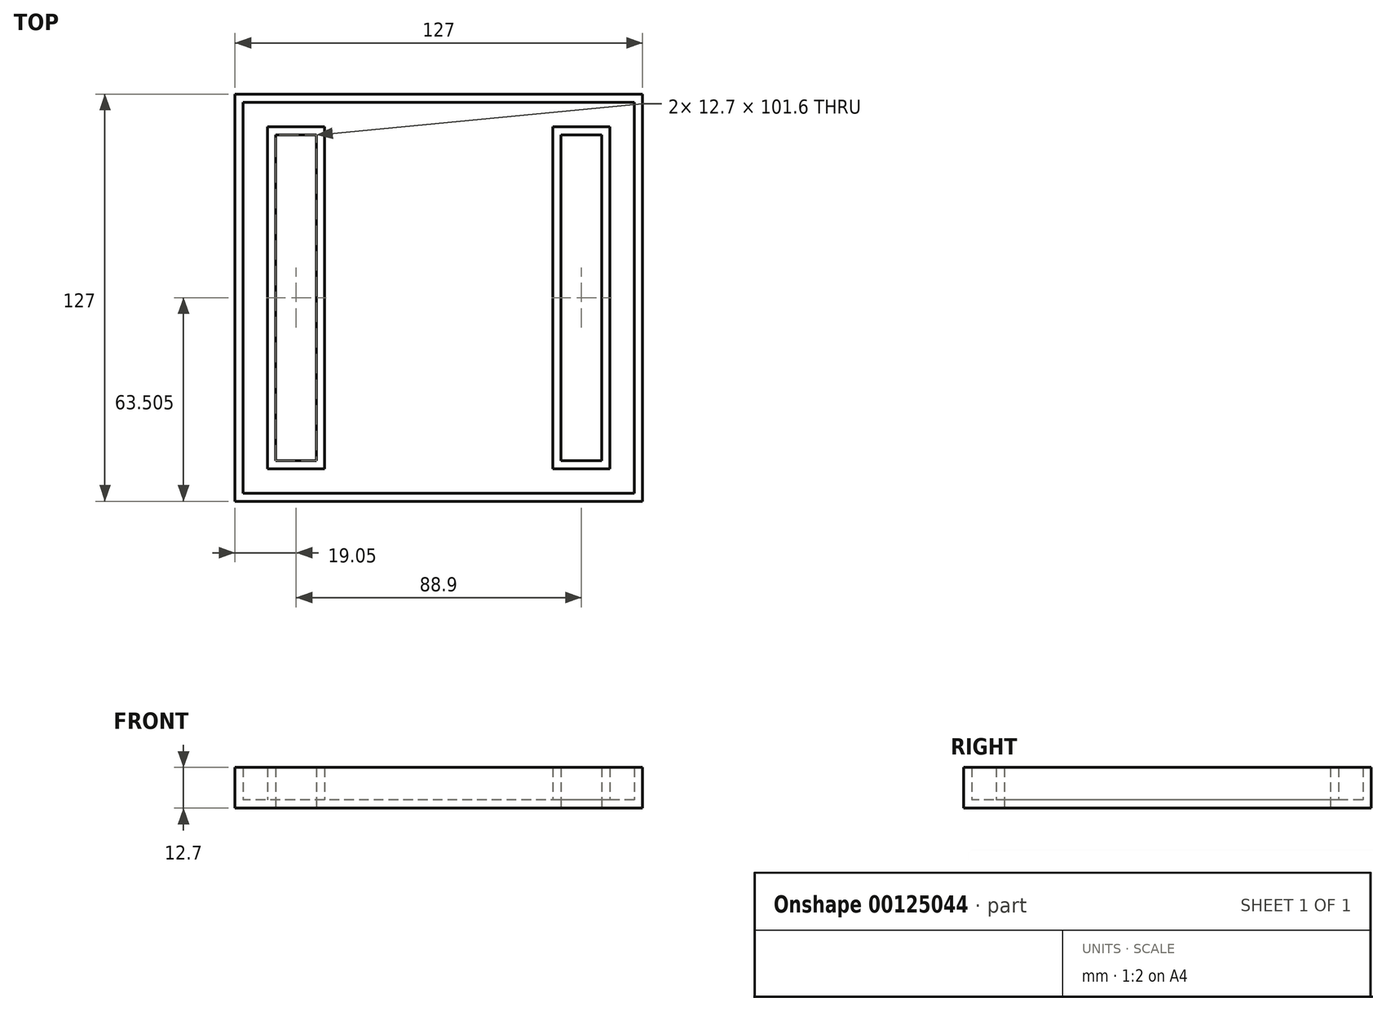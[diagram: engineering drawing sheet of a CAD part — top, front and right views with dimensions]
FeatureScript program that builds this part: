
annotation { "Feature Type Name" : "Feature", "Feature Type Description" : "" }
export const myFeature = defineFeature(function(context is Context, id is Id, definition is map)
    precondition{}
    {
        {
            var Q0;
            Q0=qCreatedBy(makeId("Top.planeOp"),FACE);
            var sketch = newSketch(context, id + "F0", { "sketchPlane" : qUnion([Q0])});
            skLineSegment(sketch, "E0", {"start": v(-50.02, 59.33) * mm, "end": v(-50.02, -67.67) * mm});
            skLineSegment(sketch, "E1", {"start": v(-50.02, -67.67) * mm, "end": v(76.98, -67.67) * mm});
            skLineSegment(sketch, "E2", {"start": v(76.98, -67.67) * mm, "end": v(76.98, 59.33) * mm});
            skLineSegment(sketch, "E3", {"start": v(76.98, 59.33) * mm, "end": v(-50.02, 59.33) * mm});
            skLineSegment(sketch, "E4", {"start": v(-37.32, 46.63) * mm, "end": v(-37.32, -54.97) * mm});
            skLineSegment(sketch, "E5", {"start": v(-37.32, -54.97) * mm, "end": v(-24.62, -54.97) * mm});
            skLineSegment(sketch, "E6", {"start": v(-24.62, -54.97) * mm, "end": v(-24.62, 46.63) * mm});
            skLineSegment(sketch, "E7", {"start": v(-24.62, 46.63) * mm, "end": v(-37.32, 46.63) * mm});
            skLineSegment(sketch, "E8", {"start": v(51.58, 46.63) * mm, "end": v(51.58, -54.97) * mm});
            skLineSegment(sketch, "E9", {"start": v(51.58, -54.97) * mm, "end": v(64.28, -54.97) * mm});
            skLineSegment(sketch, "E10", {"start": v(64.28, -54.97) * mm, "end": v(64.28, 46.63) * mm});
            skLineSegment(sketch, "E11", {"start": v(64.28, 46.63) * mm, "end": v(51.58, 46.63) * mm});
            skSolve(sketch);
        }
        {
            var Q0;
            Q0=makeQuery(id+"F0.imprint","IMPRINT",FACE,{"disambiguationData":[TD([[makeQuery(id+"F0.imprint","IMPRINT",EDGE,{"derivedFrom":sQuery(id+"F0.wireOp",EDGE,"E0")}),1.0]])]});
            extrude(context, id + "F1", {"entities" : qUnion([Q0]), "depth" : 12.7 * mm});
        }
        {
            var Q0;
            Q0=makeQuery(id+"F1.opExtrude","CAP_FACE",FACE,{"disambiguationData":[OSD([sQuery(id+"F0.wireOp",EDGE,"E0"),sQuery(id+"F0.wireOp",EDGE,"E1"),sQuery(id+"F0.wireOp",EDGE,"E2"),sQuery(id+"F0.wireOp",EDGE,"E3"),sQuery(id+"F0.wireOp",EDGE,"E4"),sQuery(id+"F0.wireOp",EDGE,"E5"),sQuery(id+"F0.wireOp",EDGE,"E6"),sQuery(id+"F0.wireOp",EDGE,"E7"),sQuery(id+"F0.wireOp",EDGE,"E8"),sQuery(id+"F0.wireOp",EDGE,"E9"),sQuery(id+"F0.wireOp",EDGE,"E10"),sQuery(id+"F0.wireOp",EDGE,"E11")])],"isStart":false});
            shell(context, id + "F2", {"entities" : qUnion([Q0]), "thickness" : 2.54 * mm});
        }
    });
